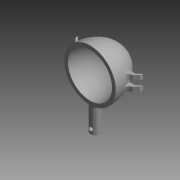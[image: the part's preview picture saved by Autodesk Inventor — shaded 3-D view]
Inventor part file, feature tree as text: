
AUTODESK INVENTOR PART (.ipt)
format: ipt  version: 2014 SP2 (Build 180246200, 246)  size: 380,928 bytes
history: native  units: mm
features: sketch x6, projected_geometry x4, extrude x3, revolve x2, plane x2, fillet x2, mirror x2, hole x1
ambient origin geometry x8: Origin, YZ Plane, XZ Plane, XY Plane, X Axis, Y Axis, Z Axis, Center Point
bodies: Solid1 (feature_tree)
feature tree (22):
  revolve  "Revolution1"  Angle=90.0deg
  plane  "Work Plane1"
  extrude  "Extrusion3"  Depth=6.0mm
  extrude  "Extrusion4"  Depth=3.0mm
  fillet  "Fillet1"  Radius=8.4mm
  mirror  "Mirror5"
  mirror  "Mirror6"
  extrude  "Extrusion5"  Depth=5.0mm
  plane  "Work Plane2"
  revolve  "Revolution2"  [1 undecoded]
  hole  "Hole1"  [1 undecoded]
  fillet  "Fillet2"  Radius=3.0mm
  sketch  "Sketch1"  dims[d2=90.0deg d5=90.0deg]
  sketch  "Sketch2"  dims[d23=0.0mm d24=6.0mm]
  sketch  "Sketch5"  dims[d25=45.0deg d26=3.0mm d27=8.4mm]
  projected_geometry  "Projected Loop2"
  sketch  "Sketch6"  dims[d28=0.0mm d29=5.0mm]
  sketch  "Sketch7"  dims[d30=10.0mm d31=56.0mm]
  sketch  "Sketch9"  dims[d32=0.0mm d36=5.0mm d37=4.0mm d38=6.0mm d39=4.0mm d40=2.0mm d41=90.0deg d42=8.0mm d43=20.594885mm d44=3.0mm]
  projected_geometry  "Projected Loop3"
  projected_geometry  "Project Cut Edges2"
  projected_geometry  "Project Cut Edges3"
note: 2 required parameter values undecoded (feature->parameter linkage not recoverable at this tier; creation-order binding heuristic only, values carry confidence <= 0.55)